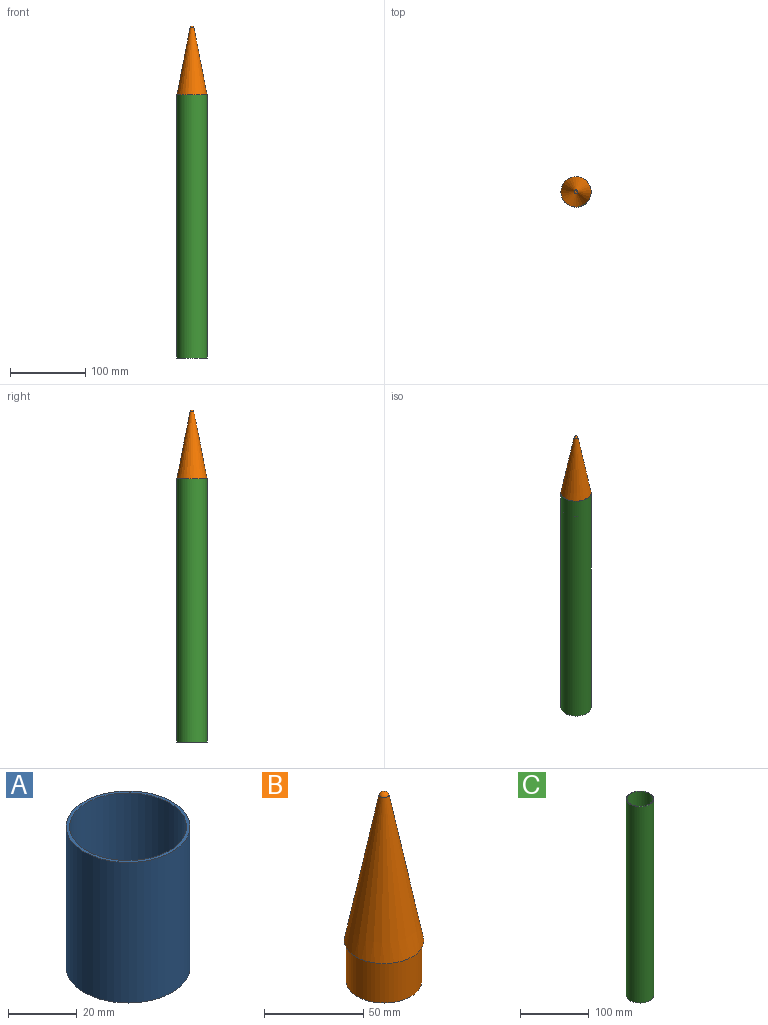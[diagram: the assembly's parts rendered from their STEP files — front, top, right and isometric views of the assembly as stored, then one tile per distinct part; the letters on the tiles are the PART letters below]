
ASSEMBLY  parts=3 mates=2
PART A: 8 faces, bbox 36x36x50 mm
  f0: plane 36x36mm, normal (0,0,1), area 110mm2, adj f1,f7
  f1: cylinder r=17mm len=34mm, axis (0,0,1), area 3204.4mm2, adj f0,f2
  f2: plane 34x34mm, normal (0,0,1), area 906.4mm2, adj f1,f3
  f3: cylinder r=0.7mm len=4mm, axis (0,0,1), area 17.6mm2, adj f2,f4
  f4: plane 34x34mm, normal (0,0,-1), area 906.4mm2, adj f3,f5
  f5: cylinder r=17mm len=34mm, axis (0,0,1), area 1709mm2, adj f4,f6
  f6: plane 36x36mm, normal (0,0,-1), area 110mm2, adj f5,f7
  f7: cylinder r=18mm len=50mm, axis (0,0,1), area 5654.9mm2, adj f0,f6
PART B: 5 faces, bbox 40x40x116.7 mm
  f0: plane 38x38mm, normal (0,0,-1), area 1134.1mm2, adj f1
  f1: cylinder r=19mm len=38mm, axis (0,0,1), area 2984.5mm2, adj f0,f2
  f2: plane 40x40mm, normal (0,0,-1), area 122.5mm2, adj f1,f3
  f3: cone r=20mm half-angle=11deg, axis (0,0,-1), area 6480.9mm2, adj f2,f4
  f4: sphere r=2.69mm, area 28.6mm2, adj f3
PART C: 4 faces, bbox 40x40x350 mm
  f0: plane 40x40mm, normal (0,0,1), area 122.5mm2, adj f1,f3
  f1: cylinder r=19mm len=350mm, axis (0,0,1), area 41783.2mm2, adj f0,f2
  f2: plane 40x40mm, normal (0,0,-1), area 122.5mm2, adj f1,f3
  f3: cylinder r=20mm len=350mm, axis (0,0,1), area 43982.3mm2, adj f0,f2
PLACE A rot(axis=(0,0,1),180deg) t=(-3.55,-0.19,106.3)mm
PLACE B rot(axis=(0,0,1),90deg) t=(-3.55,-0.19,206.3)mm
PLACE C rot(axis=(0,1,0),180deg) t=(-3.55,-0.19,-147.7)mm
MATE slider B.f3 <-> C.f1  axis (0,0,-1) through (-3.55,-0.19,206.3)mm
MATE slider A.f1 <-> C.f1  axis (0,0,-1) through (-3.55,-0.19,56.3)mm
